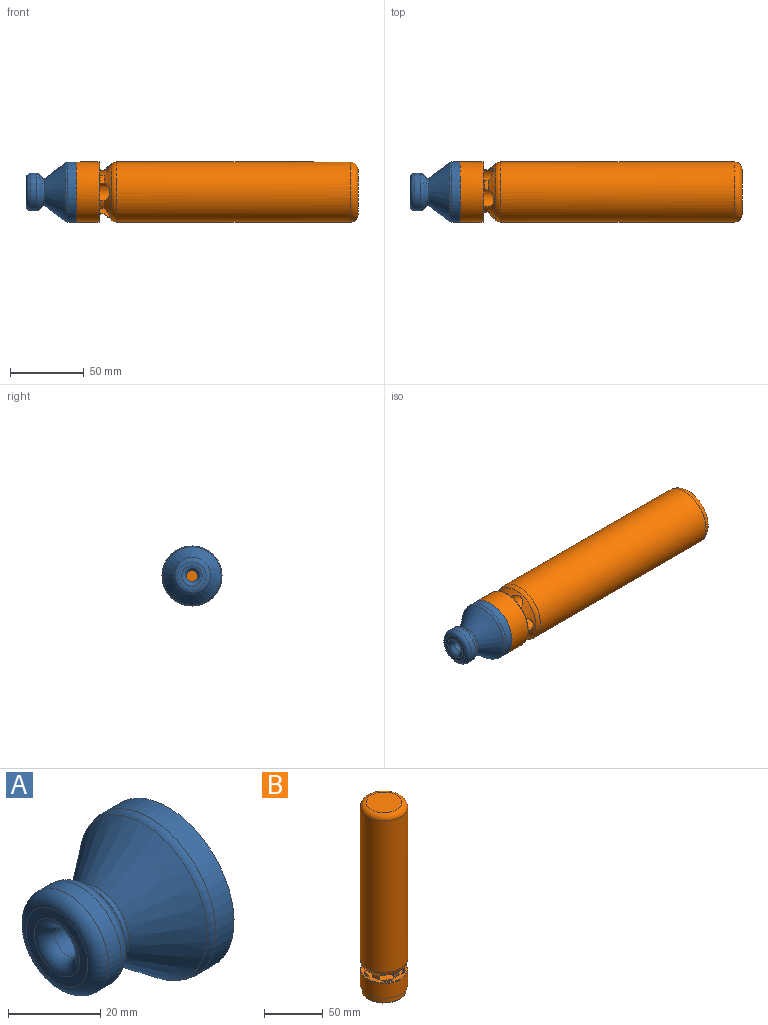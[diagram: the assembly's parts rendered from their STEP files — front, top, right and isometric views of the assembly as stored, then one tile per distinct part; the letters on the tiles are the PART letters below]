
ASSEMBLY  parts=2 mates=1
PART A: 17 faces, bbox 34x44x44 mm
  f0: cone r=8.85mm half-angle=36.7deg, axis (1,0,0), area 1572.7mm2, adj f13,f16
  f1: cone r=11.62mm half-angle=47.7deg, axis (-1,0,0), area 187.8mm2, adj f2,f16
  f2: torus R=9.48mm, axis (1,0,0), area 204.5mm2, adj f1,f3
  f3: cylinder r=12.66mm len=25.32mm, axis (1,0,0), area 310.9mm2, adj f2,f4
  f4: torus R=9.48mm, axis (1,0,0), area 360.5mm2, adj f3,f5
  f5: plane 18.97x18.97mm, normal (-1,0,0), area 129.3mm2, adj f4,f6
  f6: torus R=6.99mm, axis (1,0,0), area 155.5mm2, adj f5,f7
  f7: cylinder r=3.81mm len=7.62mm, axis (1,0,0), area 147.9mm2, adj f6,f8
  f8: torus R=6.99mm, axis (1,0,0), area 59.3mm2, adj f7,f9
  f9: cone r=18.82mm half-angle=41.7deg, axis (1,0,0), area 1549.5mm2, adj f8,f15
  f10: cylinder r=18.82mm len=37.64mm, axis (1,0,0), area 668mm2, adj f14,f15
  f11: plane 40.64x40.64mm, normal (1,0,0), area 92.3mm2, adj f12,f14
  f12: cylinder r=20.32mm len=40.64mm, axis (1,0,0), area 718.6mm2, adj f11,f13
  f13: torus R=17.14mm, axis (1,0,0), area 257.1mm2, adj f0,f12
  f14: cone r=18.82mm half-angle=45deg, axis (1,0,0), area 130mm2, adj f10,f11
  f15: torus R=18.31mm, axis (1,0,0), area 43.6mm2, adj f9,f10
  f16: torus R=10.21mm, axis (1,0,0), area 87.4mm2, adj f0,f1
PART B: 53 faces, bbox 44x44x196.9 mm
  f0: cylinder r=14.94mm len=5.94mm, axis (0,0,-1), area 14.8mm2, adj f26,f27,f28,f29
  f1: cylinder r=14.94mm len=5.05mm, axis (0,0,-1), area 14.8mm2, adj f25,f26,f30,f31
  f2: cylinder r=14.94mm len=5.05mm, axis (0,0,-1), area 14.8mm2, adj f24,f25,f32,f33
  f3: cylinder r=14.94mm len=5.94mm, axis (0,0,-1), area 14.8mm2, adj f23,f24,f34,f35
  f4: cone r=14.94mm half-angle=40deg, axis (0,0,1), area 466.7mm2, adj f23,f24,f25,f26,f27,f28,f30,f32
  f5: cylinder r=14.94mm len=6.25mm, axis (0,0,-1), area 14.8mm2, adj f23,f27,f41,f42
  f6: plane 39.62x39.62mm, normal (0,0,1), area 933.1mm2, adj f13,f14,f15,f16,f17,f18,f19,f20
  f7: cylinder r=20.32mm len=40.64mm, axis (0,0,-1), area 1962mm2, adj f8,f43
  f8: plane 40.64x40.64mm, normal (0,0,-1), area 95.5mm2, adj f7,f51
  f9: cylinder r=18.8mm len=37.59mm, axis (0,0,-1), area 599.9mm2, adj f44,f51
  f10: plane 36.58x36.58mm, normal (0,0,-1), area 955.7mm2, adj f13,f15,f18,f20,f21,f36,f37,f38
  f11: plane 30.48x30.48mm, normal (0,0,1), area 729.7mm2, adj f50
  f12: cylinder r=20.32mm len=158.23mm, axis (0,0,-1), area 20202mm2, adj f50,f52
  f13: cylinder r=6.36mm len=22.23mm, axis (0,0,-1), area 238.2mm2, adj f6,f10,f14,f40
  f14: plane 21.72x7.67mm, normal (-0.59,-0.81,0), area 206.1mm2, adj f6,f13,f40
  f15: cylinder r=6.36mm len=22.23mm, axis (0,0,-1), area 238.2mm2, adj f6,f10,f16,f39
  f16: plane 21.72x9.02mm, normal (-0.95,0.31,0), area 206.1mm2, adj f6,f15,f39
  f17: plane 21.72x9.49mm, normal (0,1,0), area 206.1mm2, adj f6,f18,f38
  f18: cylinder r=6.36mm len=22.23mm, axis (0,0,-1), area 238.2mm2, adj f6,f10,f17,f38
  f19: plane 21.72x9.03mm, normal (0.95,0.31,0), area 206.1mm2, adj f6,f20,f37
  f20: cylinder r=6.36mm len=22.23mm, axis (0,0,-1), area 238.2mm2, adj f6,f10,f19,f37
  f21: cylinder r=6.36mm len=22.23mm, axis (0,0,-1), area 238.2mm2, adj f6,f10,f22,f36
  f22: plane 21.72x7.68mm, normal (0.59,-0.81,0), area 206.1mm2, adj f6,f21,f36
  f23: cylinder r=6.35mm len=164.47mm, axis (0,0,-1), area 6473mm2, adj f3,f4,f5,f6,f34,f35,f41,f42
  f24: cylinder r=6.35mm len=76.2mm, axis (0,0,-1), area 2951.4mm2, adj f2,f3,f4,f6,f32,f33,f34,f35
  f25: cylinder r=6.35mm len=92.08mm, axis (0,0,-1), area 3584.8mm2, adj f1,f2,f4,f6,f30,f31,f32,f33
  f26: cylinder r=6.35mm len=130.18mm, axis (0,0,-1), area 5104.9mm2, adj f0,f1,f4,f6,f28,f29,f30,f31
  f27: cylinder r=6.35mm len=106.05mm, axis (0,0,-1), area 4142.2mm2, adj f0,f4,f5,f6,f28,f29,f41,f42
  f28: torus R=15.44mm, axis (0,0,-1), area 2.3mm2, adj f0,f4,f26,f27
  f29: torus R=15.44mm, axis (0,0,1), area 5.4mm2, adj f0,f6,f26,f27
  f30: torus R=15.44mm, axis (0,0,-1), area 2.3mm2, adj f1,f4,f25,f26
  f31: torus R=15.44mm, axis (0,0,1), area 5.4mm2, adj f1,f6,f25,f26
  f32: torus R=15.44mm, axis (0,0,-1), area 2.3mm2, adj f2,f4,f24,f25
  f33: torus R=15.44mm, axis (0,0,1), area 5.4mm2, adj f2,f6,f24,f25
  f34: torus R=15.44mm, axis (0,0,-1), area 2.3mm2, adj f3,f4,f23,f24
  f35: torus R=15.44mm, axis (0,0,1), area 5.4mm2, adj f3,f6,f23,f24
  f36: cylinder r=0.51mm len=8.64mm, axis (-0.81,-0.59,0), area 7.8mm2, adj f10,f21,f22
  f37: cylinder r=0.51mm len=9.96mm, axis (0.31,-0.95,0), area 7.8mm2, adj f10,f19,f20
  f38: cylinder r=0.51mm len=10.31mm, axis (1,0,0), area 7.8mm2, adj f10,f17,f18
  f39: cylinder r=0.51mm len=9.96mm, axis (0.31,0.95,0), area 7.8mm2, adj f10,f15,f16
  f40: cylinder r=0.51mm len=8.63mm, axis (-0.81,0.59,0), area 7.8mm2, adj f10,f13,f14
  f41: torus R=15.44mm, axis (0,0,-1), area 2.3mm2, adj f4,f5,f23,f27
  f42: torus R=15.44mm, axis (0,0,1), area 5.4mm2, adj f5,f6,f23,f27
  f43: torus R=19.81mm, axis (0,0,1), area 101mm2, adj f6,f7
  f44: torus R=18.29mm, axis (0,0,-1), area 93.3mm2, adj f9,f10
  f45: sphere r=6.35mm, area 253.4mm2, adj f24
  f46: sphere r=6.35mm, area 253.4mm2, adj f25
  f47: sphere r=6.35mm, area 253.4mm2, adj f27
  f48: sphere r=6.35mm, area 253.4mm2, adj f26
  f49: sphere r=6.35mm, area 253.4mm2, adj f23
  f50: torus R=15.24mm, axis (0,0,-1), area 926.2mm2, adj f11,f12
  f51: cone r=18.8mm half-angle=45deg, axis (0,0,1), area 129.8mm2, adj f8,f9
  f52: torus R=15.24mm, axis (0,0,1), area 443.8mm2, adj f4,f12
PLACE A t=(-25.33,-8.89,-89.79)mm
PLACE B rot(axis=(0.71,0,0.71),180deg) t=(-32.59,-8.89,-89.79)mm
MATE planar B.f0 <-> A.f0  axis (-1,0,0) through (-26.24,-8.89,-89.79)mm
